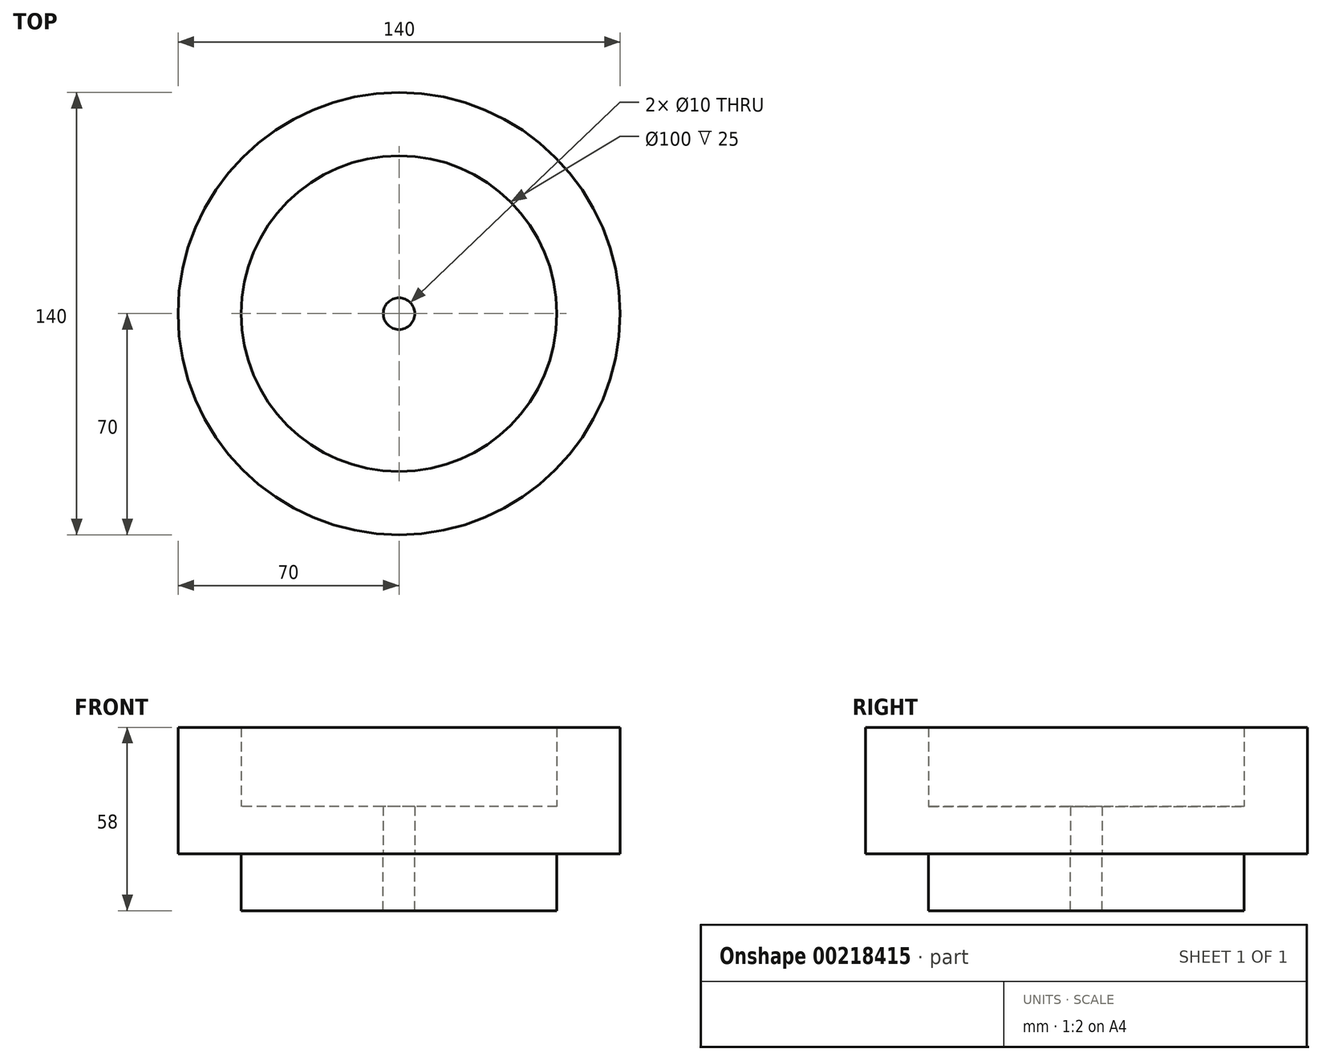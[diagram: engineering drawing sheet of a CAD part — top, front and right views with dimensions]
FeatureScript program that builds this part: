
annotation { "Feature Type Name" : "Feature", "Feature Type Description" : "" }
export const myFeature = defineFeature(function(context is Context, id is Id, definition is map)
    precondition{}
    {
        {
            var Q0;
            Q0=qCreatedBy(makeId("Top.planeOp"),FACE);
            var sketch = newSketch(context, id + "F0", { "sketchPlane" : qUnion([Q0])});
            skCircle(sketch, "E0", {"center": v(0, 0) * mm, "radius": 50 * mm});
            skCircle(sketch, "E1", {"center": v(0, 0) * mm, "radius": 70 * mm});
            skCircle(sketch, "E2", {"center": v(0, 0) * mm, "radius": 5 * mm});
            skSolve(sketch);
        }
        {
            var Q0;
            Q0=makeQuery(id+"F0.imprint","IMPRINT",FACE,{"disambiguationData":[TD([[makeQuery(id+"F0.imprint","IMPRINT",EDGE,{"derivedFrom":sQuery(id+"F0.wireOp",EDGE,"E0")}),-1.0]])]});
            extrude(context, id + "F1", {"entities" : qUnion([Q0]), "depth" : 40 * mm, "offsetDistance" : 25 * mm});
        }
        {
            var Q0;
            Q0=makeQuery(id+"F0.imprint","IMPRINT",FACE,{"disambiguationData":[TD([[makeQuery(id+"F0.imprint","IMPRINT",EDGE,{"derivedFrom":sQuery(id+"F0.wireOp",EDGE,"E0")}),1.0]])]});
            extrude(context, id + "F2", {"entities" : qUnion([Q0]), "operationType" : NewBodyOperationType.ADD, "depth" : 15 * mm, "offsetDistance" : 25 * mm});
        }
        {
            var Q0;
            Q0=makeQuery(id+"F0.imprint","IMPRINT",FACE,{"disambiguationData":[TD([[makeQuery(id+"F0.imprint","IMPRINT",EDGE,{"derivedFrom":sQuery(id+"F0.wireOp",EDGE,"E0")}),1.0]])]});
            extrude(context, id + "F3", {"entities" : qUnion([Q0]), "oppositeDirection" : true, "depth" : 18 * mm, "offsetDistance" : 25 * mm});
        }
    });
